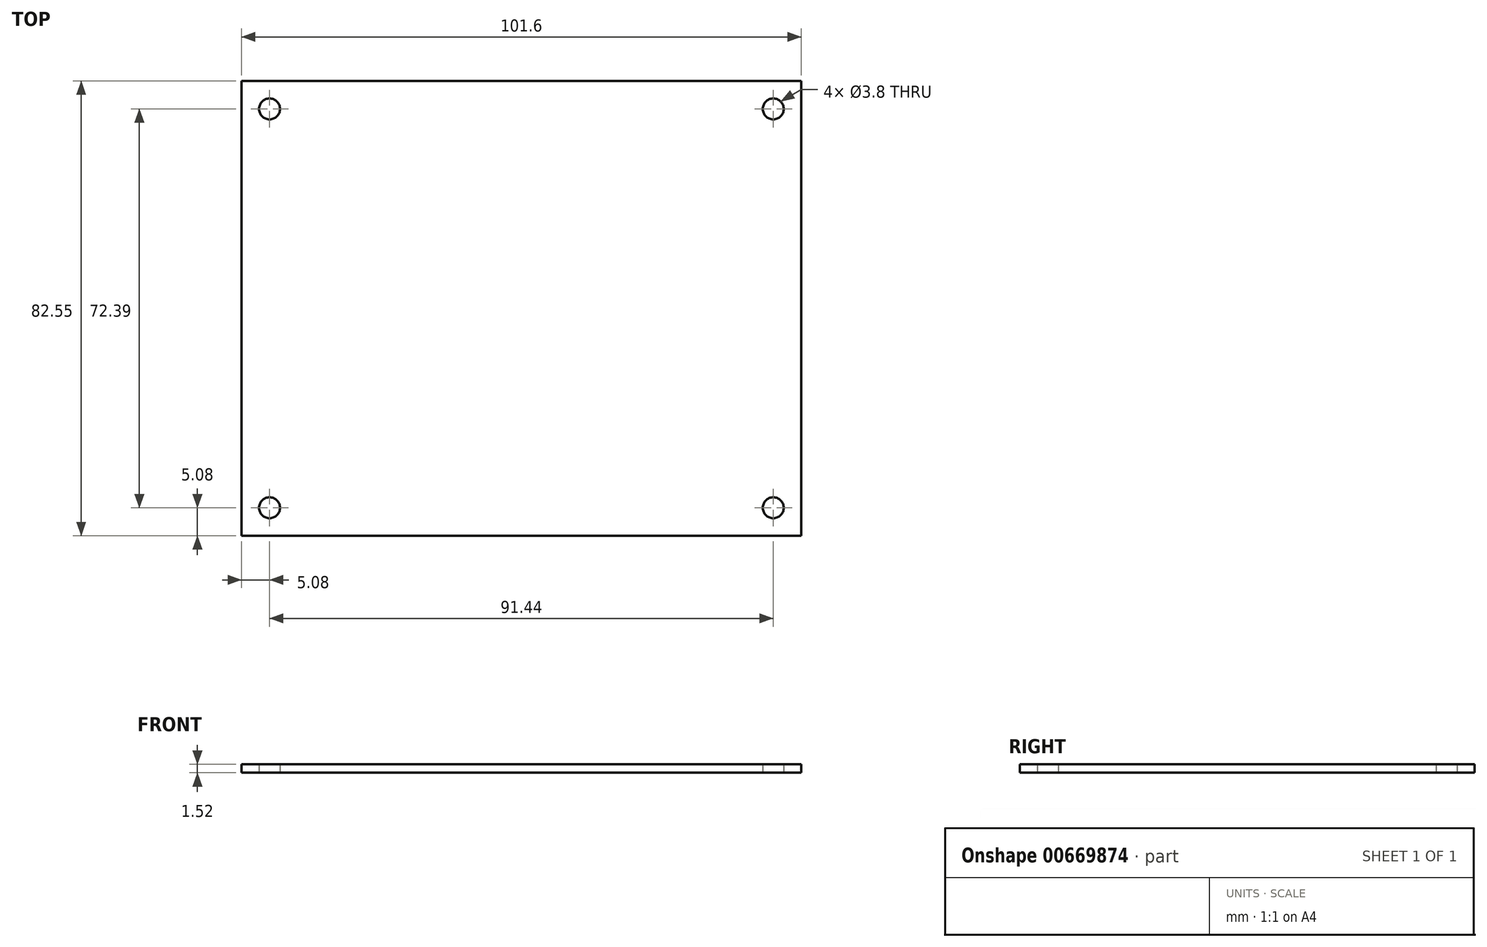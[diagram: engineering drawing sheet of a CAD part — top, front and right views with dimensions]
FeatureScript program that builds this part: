
annotation { "Feature Type Name" : "Feature", "Feature Type Description" : "" }
export const myFeature = defineFeature(function(context is Context, id is Id, definition is map)
    precondition{}
    {
        {
            var Q0;
            Q0=qCreatedBy(makeId("Top.planeOp"),FACE);
            var sketch = newSketch(context, id + "F0", { "sketchPlane" : qUnion([Q0])});
            skLineSegment(sketch, "E0.bottom", {"start": v(0, 0) * mm, "end": v(101.6, 0) * mm});
            skLineSegment(sketch, "E0.top", {"start": v(0, 82.55) * mm, "end": v(101.6, 82.55) * mm});
            skLineSegment(sketch, "E0.left", {"start": v(0, 0) * mm, "end": v(0, 82.55) * mm});
            skLineSegment(sketch, "E0.right", {"start": v(101.6, 0) * mm, "end": v(101.6, 82.55) * mm});
            skSolve(sketch);
        }
        {
            var Q0;
            Q0=qSketchRegion(id+"F0",true);
            extrude(context, id + "F1", {"entities" : qUnion([Q0]), "depth" : 1.52 * mm});
        }
        {
            var Q0;
            Q0=makeQuery(id+"F1.opExtrude","CAP_FACE",FACE,{"disambiguationData":[OSD([sQuery(id+"F0.wireOp",EDGE,"E0.bottom"),sQuery(id+"F0.wireOp",EDGE,"E0.top"),sQuery(id+"F0.wireOp",EDGE,"E0.left"),sQuery(id+"F0.wireOp",EDGE,"E0.right")])],"isStart":false});
            var sketch = newSketch(context, id + "F2", { "sketchPlane" : qUnion([Q0])});
            skPoint(sketch, "E1", {"position": v(5.08, 77.47) * mm});
            skPoint(sketch, "E2", {"position": v(96.52, 77.47) * mm});
            skPoint(sketch, "E3", {"position": v(96.52, 5.08) * mm});
            skPoint(sketch, "E4", {"position": v(5.08, 5.08) * mm});
            skSolve(sketch);
        }
        {
            var Q0;
            Q0=sQuery(id+"F2.wireOp",VERTEX,"E1");
            var Q1;
            Q1=sQuery(id+"F2.wireOp",VERTEX,"E2");
            var Q2;
            Q2=sQuery(id+"F2.wireOp",VERTEX,"E4");
            var Q3;
            Q3=sQuery(id+"F2.wireOp",VERTEX,"E3");
            var Q4;
            Q4=makeQuery(id+"F1.opExtrude","SWEPT_BODY",BODY,{"disambiguationData":[OSD([sQuery(id+"F0.wireOp",EDGE,"E0.bottom"),sQuery(id+"F0.wireOp",EDGE,"E0.top"),sQuery(id+"F0.wireOp",EDGE,"E0.left"),sQuery(id+"F0.wireOp",EDGE,"E0.right")])]});
            hole(context, id + "F3", {"style" : HoleStyle.SIMPLE, "endStyle" : HoleEndStyle.THROUGH, "standardTappedOrClearance" : lookupTablePath({ "standard" : "ANSI", "fit" : "Normal (ASME)", "size" : "#6", "type" : "Clearance" }), "standardBlindInLast" : lookupTablePath({ "fit" : "Free", "standard" : "ANSI", "size" : "#6", "type" : "Clearance" }), "holeDiameter" : 3.8 * mm, "isTappedThrough" : true, "tappedDepth" : 2.4 * mm, "tapClearance" : 3, "startFromSketch" : true, "locations" : qUnion([Q0, Q1, Q2, Q3]), "scope" : qUnion([Q4])});
        }
    });
